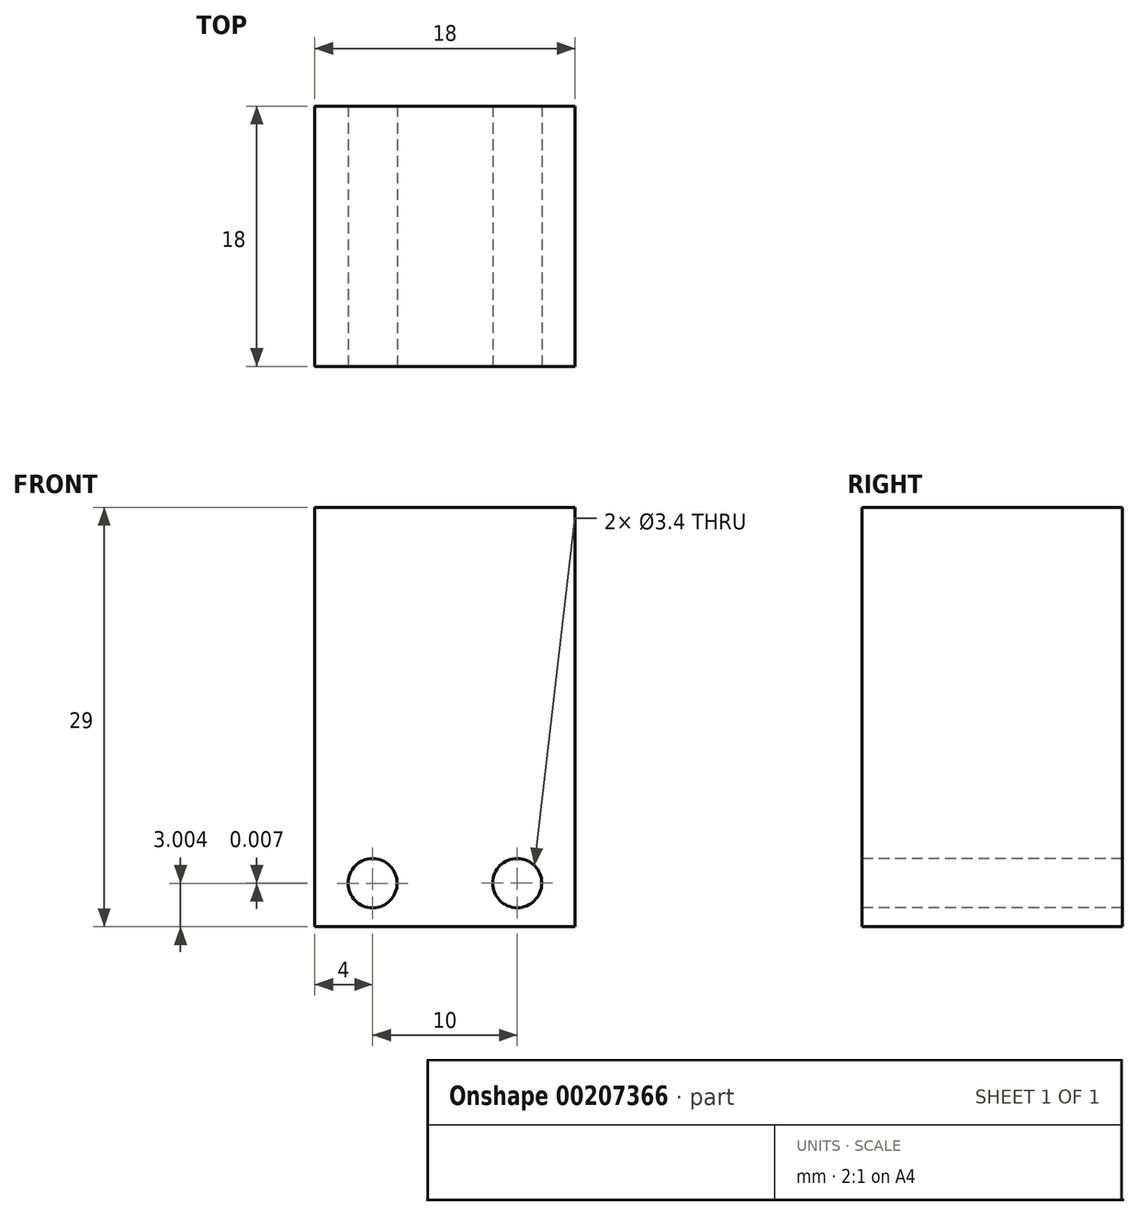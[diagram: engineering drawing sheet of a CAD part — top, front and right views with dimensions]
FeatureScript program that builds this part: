
annotation { "Feature Type Name" : "Feature", "Feature Type Description" : "" }
export const myFeature = defineFeature(function(context is Context, id is Id, definition is map)
    precondition{}
    {
        {
            var Q0;
            Q0=qCreatedBy(makeId("Front.planeOp"),FACE);
            var sketch = newSketch(context, id + "F0", { "sketchPlane" : qUnion([Q0])});
            skLineSegment(sketch, "E0.bottom", {"start": v(-9, 12.13) * mm, "end": v(9, 12.13) * mm});
            skLineSegment(sketch, "E0.top", {"start": v(-9, -16.87) * mm, "end": v(9, -16.87) * mm});
            skLineSegment(sketch, "E0.left", {"start": v(-9, 12.13) * mm, "end": v(-9, -16.87) * mm});
            skLineSegment(sketch, "E0.right", {"start": v(9, 12.13) * mm, "end": v(9, -16.87) * mm});
            skPoint(sketch, "E1", {"position": v(-5, -13.87) * mm});
            skPoint(sketch, "E2", {"position": v(5, -13.86) * mm});
            skLineSegment(sketch, "E3", {"start": v(-5, -13.87) * mm, "end": v(5, -13.86) * mm, "construction": true});
            skPoint(sketch, "E4", {"position": v(0, -13.86) * mm});
            skPoint(sketch, "E5", {"position": v(0, 12.13) * mm});
            skSolve(sketch);
        }
        {
            var Q0;
            Q0=makeQuery(id+"F0.imprint","IMPRINT",FACE,{"disambiguationData":[TD([[makeQuery(id+"F0.imprint","IMPRINT",EDGE,{"derivedFrom":sQuery(id+"F0.wireOp",EDGE,"E0.bottom")}),-1.0]])]});
            extrude(context, id + "F1", {"entities" : qUnion([Q0]), "depth" : 18 * mm, "offsetDistance" : 25 * mm});
        }
        {
            var Q0;
            Q0=sQuery(id+"F0.wireOp",VERTEX,"E1");
            var Q1;
            Q1=sQuery(id+"F0.wireOp",VERTEX,"E2");
            var Q2;
            Q2=makeQuery(id+"F1.opExtrude","SWEPT_BODY",BODY,{"disambiguationData":[OSD([sQuery(id+"F0.wireOp",EDGE,"E0.bottom"),sQuery(id+"F0.wireOp",EDGE,"E0.top"),sQuery(id+"F0.wireOp",EDGE,"E0.left"),sQuery(id+"F0.wireOp",EDGE,"E0.right")])]});
            hole(context, id + "F2", {"style" : HoleStyle.SIMPLE, "endStyle" : HoleEndStyle.THROUGH, "oppositeDirection" : true, "standardTappedOrClearance" : lookupTablePath({ "fit" : "Normal", "standard" : "ISO", "size" : "M3", "type" : "Clearance" }), "standardBlindInLast" : lookupTablePath({ "fit" : "Normal", "standard" : "ISO", "engagement" : "75%", "pitch" : "0.5 mm", "size" : "M3", "type" : "Clearance & tapped" }), "holeDiameter" : 3.4 * mm, "majorDiameter" : 5 * mm, "isTappedThrough" : true, "tappedDepth" : 12 * mm, "tapClearance" : 3, "locations" : qUnion([Q0, Q1]), "scope" : qUnion([Q2]), "startStyle" : HoleStartStyle.PART});
        }
    });
